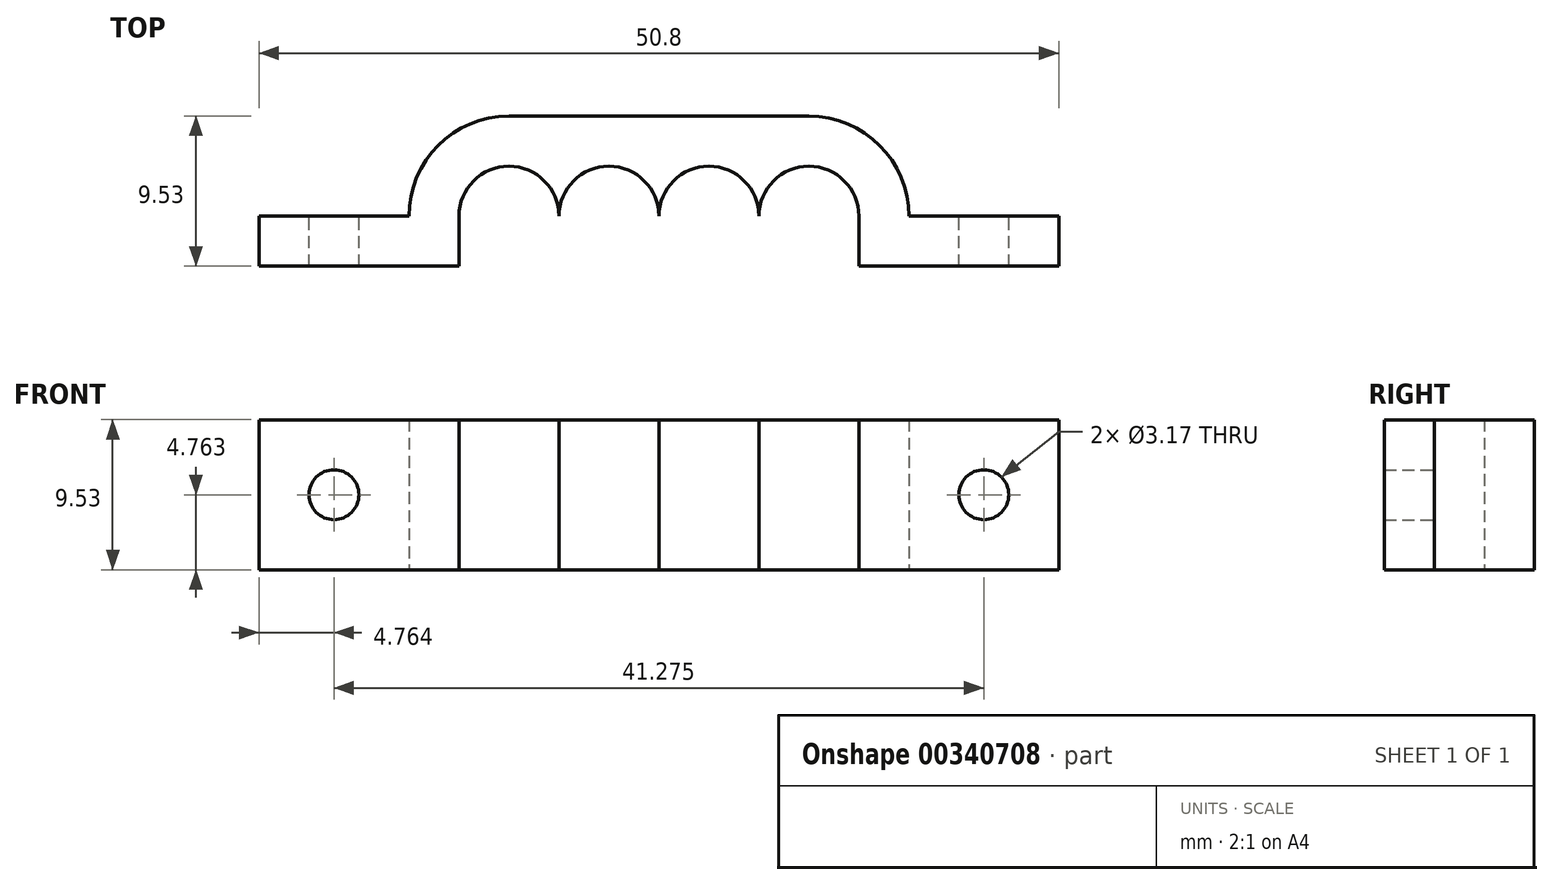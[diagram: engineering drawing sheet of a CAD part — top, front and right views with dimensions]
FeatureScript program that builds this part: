
annotation { "Feature Type Name" : "Feature", "Feature Type Description" : "" }
export const myFeature = defineFeature(function(context is Context, id is Id, definition is map)
    precondition{}
    {
        {
            var Q0;
            Q0=qCreatedBy(makeId("Top.planeOp"),FACE);
            var sketch = newSketch(context, id + "F0", { "sketchPlane" : qUnion([Q0])});
            skLineSegment(sketch, "E0.bottom", {"start": v(41.86, -44.45) * mm, "end": v(-8.94, -44.45) * mm});
            skCircle(sketch, "E1", {"center": v(6.94, -41.28) * mm, "radius": 3.18 * mm});
            skCircle(sketch, "E2", {"center": v(13.29, -41.28) * mm, "radius": 3.18 * mm});
            skCircle(sketch, "E3", {"center": v(19.64, -41.28) * mm, "radius": 3.18 * mm});
            skCircle(sketch, "E4", {"center": v(25.99, -41.27) * mm, "radius": 3.18 * mm});
            skLineSegment(sketch, "E5.bottom", {"start": v(-8.94, -44.45) * mm, "end": v(41.86, -44.45) * mm});
            skLineSegment(sketch, "E5.top", {"start": v(-8.94, -41.28) * mm, "end": v(41.86, -41.28) * mm});
            skLineSegment(sketch, "E6", {"start": v(3.76, -41.28) * mm, "end": v(3.76, -44.45) * mm});
            skLineSegment(sketch, "E7", {"start": v(29.16, -41.28) * mm, "end": v(29.16, -44.45) * mm});
            skLineSegment(sketch, "E8.bottom", {"start": v(0.59, -44.45) * mm, "end": v(32.34, -44.45) * mm});
            skLineSegment(sketch, "E8.top", {"start": v(6.94, -34.93) * mm, "end": v(25.99, -34.93) * mm});
            skLineSegment(sketch, "E8.left", {"start": v(0.59, -44.45) * mm, "end": v(0.59, -41.28) * mm});
            skLineSegment(sketch, "E8.right", {"start": v(32.34, -44.45) * mm, "end": v(32.34, -41.28) * mm});
            skPoint(sketch, "E9.visualSharp", {"position": v(0.59, -34.93) * mm});
            skArc(sketch, "E9.filletArc", {"start": v(6.94, -34.92) * mm, "mid": v(2.45, -36.78) * mm, "end": v(0.59, -41.28) * mm});
            skPoint(sketch, "E10.visualSharp", {"position": v(32.34, -34.93) * mm});
            skArc(sketch, "E10.filletArc", {"start": v(32.34, -41.28) * mm, "mid": v(30.48, -36.78) * mm, "end": v(25.99, -34.92) * mm});
            skLineSegment(sketch, "E11", {"start": v(-2.59, -28.58) * mm, "end": v(35.51, -28.58) * mm});
            skLineSegment(sketch, "E12", {"start": v(-8.94, -44.45) * mm, "end": v(-8.94, -34.93) * mm});
            skLineSegment(sketch, "E13", {"start": v(41.86, -44.45) * mm, "end": v(41.86, -34.93) * mm});
            skPoint(sketch, "E14.visualSharp", {"position": v(-8.94, -28.58) * mm});
            skArc(sketch, "E14.filletArc", {"start": v(-2.59, -28.57) * mm, "mid": v(-7.08, -30.43) * mm, "end": v(-8.94, -34.93) * mm});
            skPoint(sketch, "E15.visualSharp", {"position": v(41.86, -28.58) * mm});
            skArc(sketch, "E15.filletArc", {"start": v(41.86, -34.93) * mm, "mid": v(40, -30.43) * mm, "end": v(35.51, -28.57) * mm});
            skSolve(sketch);
        }
        {
            var Q0;
            {var subQ0=sQuery(id+"F0.wireOp",EDGE,"E12");var subQ5=sQuery(id+"F0.wireOp",EDGE,"E5.top");var subQ6=makeQuery(id+"F0.imprint","INTERSECT",VERTEX,{"derivedFrom":[subQ5,subQ0]});Q0=makeQuery(id+"F0.imprint","IMPRINT",FACE,{"disambiguationData":[TD([[makeQuery(id+"F0.imprint","IMPRINT",EDGE,{"disambiguationData":[TD([[subQ6,-1.0]])],"derivedFrom":subQ5}),-1.0]])]});}
            var Q1;
            {var subQ0=sQuery(id+"F0.wireOp",EDGE,"E6");Q1=makeQuery(id+"F0.imprint","IMPRINT",FACE,{"disambiguationData":[TD([[makeQuery(id+"F0.imprint","IMPRINT",EDGE,{"derivedFrom":subQ0}),-1.0]])]});}
            var Q2;
            Q2=makeQuery(id+"F0.imprint","IMPRINT",FACE,{"disambiguationData":[TD([[makeQuery(id+"F0.imprint","IMPRINT",EDGE,{"derivedFrom":sQuery(id+"F0.wireOp",EDGE,"E8.top")}),-1.0]])]});
            var Q3;
            {var subQ0=sQuery(id+"F0.wireOp",EDGE,"E7");Q3=makeQuery(id+"F0.imprint","IMPRINT",FACE,{"disambiguationData":[TD([[makeQuery(id+"F0.imprint","IMPRINT",EDGE,{"derivedFrom":subQ0}),1.0]])]});}
            var Q4;
            {var subQ0=sQuery(id+"F0.wireOp",EDGE,"E13");var subQ5=sQuery(id+"F0.wireOp",EDGE,"E5.top");var subQ6=makeQuery(id+"F0.imprint","INTERSECT",VERTEX,{"derivedFrom":[subQ5,subQ0]});Q4=makeQuery(id+"F0.imprint","IMPRINT",FACE,{"disambiguationData":[TD([[makeQuery(id+"F0.imprint","IMPRINT",EDGE,{"disambiguationData":[TD([[subQ6,1.0]])],"derivedFrom":subQ5}),-1.0]])]});}
            extrude(context, id + "F1", {"entities" : qUnion([Q0, Q1, Q2, Q3, Q4]), "depth" : 9.52 * mm});
        }
        {
            var Q0;
            {var subQ0=sQuery(id+"F0.wireOp",EDGE,"E5.top");Q0=makeQuery(id+"F1.opExtrude","SWEPT_FACE",FACE,{"disambiguationData":[OSD([subQ0]),TDD([makeQuery(id+"F0.imprint","IMPRINT",EDGE,{"disambiguationData":[TD([[makeQuery(id+"F0.imprint","INTERSECT",VERTEX,{"derivedFrom":[subQ0,sQuery(id+"F0.wireOp",EDGE,"E12")]}),-1.0]])],"derivedFrom":subQ0})])]});}
            var sketch = newSketch(context, id + "F2", { "sketchPlane" : qUnion([Q0])});
            skCircle(sketch, "E16", {"center": v(4.18, 4.76) * mm, "radius": 1.59 * mm});
            skPoint(sketch, "E16.centerSnap0", {"position": v(4.18, 9.53) * mm});
            skPoint(sketch, "E16.centerSnap1", {"position": v(8.94, 4.76) * mm});
            skSolve(sketch);
        }
        {
            var Q0;
            {var subQ0=sQuery(id+"F0.wireOp",EDGE,"E5.top");Q0=makeQuery(id+"F1.opExtrude","SWEPT_FACE",FACE,{"disambiguationData":[OSD([subQ0]),TDD([makeQuery(id+"F0.imprint","IMPRINT",EDGE,{"disambiguationData":[TD([[makeQuery(id+"F0.imprint","INTERSECT",VERTEX,{"derivedFrom":[subQ0,sQuery(id+"F0.wireOp",EDGE,"E13")]}),1.0]])],"derivedFrom":subQ0})])]});}
            var sketch = newSketch(context, id + "F3", { "sketchPlane" : qUnion([Q0])});
            skCircle(sketch, "E17", {"center": v(-37.1, 4.76) * mm, "radius": 1.59 * mm});
            skPoint(sketch, "E17.centerSnap0", {"position": v(-41.86, 4.76) * mm});
            skPoint(sketch, "E17.centerSnap1", {"position": v(-37.1, 9.53) * mm});
            skSolve(sketch);
        }
        {
            var Q0;
            Q0=makeQuery(id+"F2.imprint","IMPRINT",FACE,{"disambiguationData":[TD([[makeQuery(id+"F2.imprint","IMPRINT",EDGE,{"derivedFrom":sQuery(id+"F2.wireOp",EDGE,"E16")}),1.0]])]});
            var Q1;
            Q1=makeQuery(id+"F3.imprint","IMPRINT",FACE,{"disambiguationData":[TD([[makeQuery(id+"F3.imprint","IMPRINT",EDGE,{"derivedFrom":sQuery(id+"F3.wireOp",EDGE,"E17")}),1.0]])]});
            extrude(context, id + "F4", {"entities" : qUnion([Q0, Q1]), "operationType" : NewBodyOperationType.REMOVE, "oppositeDirection" : true, "depth" : 25.4 * mm});
        }
    });
